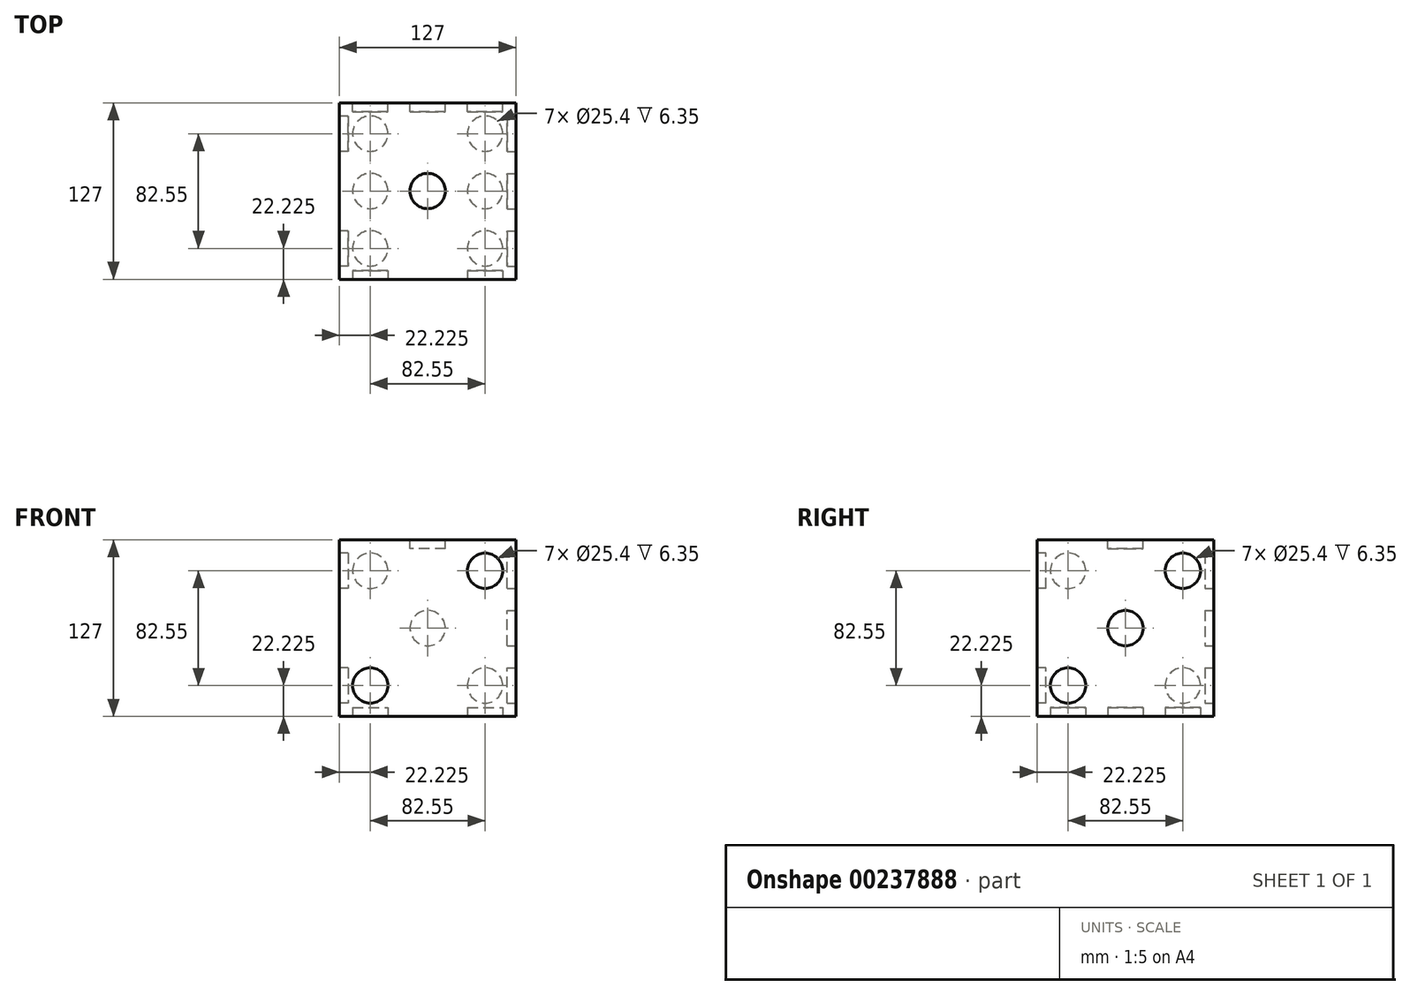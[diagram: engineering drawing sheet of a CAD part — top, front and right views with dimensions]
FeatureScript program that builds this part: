
annotation { "Feature Type Name" : "Feature", "Feature Type Description" : "" }
export const myFeature = defineFeature(function(context is Context, id is Id, definition is map)
    precondition{}
    {
        {
            var Q0;
            Q0=qCreatedBy(makeId("Top.planeOp"),FACE);
            var sketch = newSketch(context, id + "F0", { "sketchPlane" : qUnion([Q0])});
            skLineSegment(sketch, "E0.bottom", {"start": v(0, 0) * mm, "end": v(127, 0) * mm});
            skLineSegment(sketch, "E0.top", {"start": v(0, 127) * mm, "end": v(127, 127) * mm});
            skLineSegment(sketch, "E0.left", {"start": v(0, 0) * mm, "end": v(0, 127) * mm});
            skLineSegment(sketch, "E0.right", {"start": v(127, 0) * mm, "end": v(127, 127) * mm});
            skSolve(sketch);
        }
        {
            var Q0;
            Q0=makeQuery(id+"F0.imprint","IMPRINT",FACE,{"disambiguationData":[TD([[makeQuery(id+"F0.imprint","IMPRINT",EDGE,{"derivedFrom":sQuery(id+"F0.wireOp",EDGE,"E0.bottom")}),1.0]])]});
            extrude(context, id + "F1", {"entities" : qUnion([Q0]), "depth" : 127 * mm});
        }
        {
            var Q0;
            Q0=makeQuery(id+"F1.opExtrude","CAP_FACE",FACE,{"disambiguationData":[OSD([sQuery(id+"F0.wireOp",EDGE,"E0.bottom"),sQuery(id+"F0.wireOp",EDGE,"E0.top"),sQuery(id+"F0.wireOp",EDGE,"E0.left"),sQuery(id+"F0.wireOp",EDGE,"E0.right")])],"isStart":false});
            var sketch = newSketch(context, id + "F2", { "sketchPlane" : qUnion([Q0])});
            skCircle(sketch, "E1", {"center": v(63.5, 63.5) * mm, "radius": 12.7 * mm});
            skSolve(sketch);
        }
        {
            var Q0;
            Q0=makeQuery(id+"F2.imprint","IMPRINT",FACE,{"disambiguationData":[TD([[makeQuery(id+"F2.imprint","IMPRINT",EDGE,{"derivedFrom":sQuery(id+"F2.wireOp",EDGE,"E1")}),1.0]])]});
            extrude(context, id + "F3", {"entities" : qUnion([Q0]), "operationType" : NewBodyOperationType.REMOVE, "oppositeDirection" : true, "depth" : 6.35 * mm});
        }
        {
            var Q0;
            Q0=makeQuery(id+"F1.opExtrude","SWEPT_FACE",FACE,{"disambiguationData":[OSD([sQuery(id+"F0.wireOp",EDGE,"E0.bottom")])]});
            var sketch = newSketch(context, id + "F4", { "sketchPlane" : qUnion([Q0])});
            skCircle(sketch, "E2", {"center": v(104.78, 104.78) * mm, "radius": 12.7 * mm});
            skCircle(sketch, "E3", {"center": v(22.23, 22.22) * mm, "radius": 12.7 * mm});
            skSolve(sketch);
        }
        {
            var Q0;
            Q0=makeQuery(id+"F4.imprint","IMPRINT",FACE,{"disambiguationData":[TD([[makeQuery(id+"F4.imprint","IMPRINT",EDGE,{"derivedFrom":sQuery(id+"F4.wireOp",EDGE,"E3")}),1.0]])]});
            var Q1;
            Q1=makeQuery(id+"F4.imprint","IMPRINT",FACE,{"disambiguationData":[TD([[makeQuery(id+"F4.imprint","IMPRINT",EDGE,{"derivedFrom":sQuery(id+"F4.wireOp",EDGE,"E2")}),1.0]])]});
            extrude(context, id + "F5", {"entities" : qUnion([Q0, Q1]), "operationType" : NewBodyOperationType.REMOVE, "oppositeDirection" : true, "depth" : 6.35 * mm});
        }
        {
            var Q0;
            Q0=makeQuery(id+"F1.opExtrude","SWEPT_FACE",FACE,{"disambiguationData":[OSD([sQuery(id+"F0.wireOp",EDGE,"E0.left")])]});
            var sketch = newSketch(context, id + "F6", { "sketchPlane" : qUnion([Q0])});
            skCircle(sketch, "E4", {"center": v(-104.78, 22.22) * mm, "radius": 12.7 * mm});
            skCircle(sketch, "E5", {"center": v(-104.78, 104.78) * mm, "radius": 12.7 * mm});
            skCircle(sketch, "E6", {"center": v(-22.23, 104.78) * mm, "radius": 12.7 * mm});
            skCircle(sketch, "E7", {"center": v(-22.23, 22.22) * mm, "radius": 12.7 * mm});
            skSolve(sketch);
        }
        {
            var Q0;
            Q0=makeQuery(id+"F6.imprint","IMPRINT",FACE,{"disambiguationData":[TD([[makeQuery(id+"F6.imprint","IMPRINT",EDGE,{"derivedFrom":sQuery(id+"F6.wireOp",EDGE,"E5")}),1.0]])]});
            var Q1;
            Q1=makeQuery(id+"F6.imprint","IMPRINT",FACE,{"disambiguationData":[TD([[makeQuery(id+"F6.imprint","IMPRINT",EDGE,{"derivedFrom":sQuery(id+"F6.wireOp",EDGE,"E6")}),1.0]])]});
            var Q2;
            Q2=makeQuery(id+"F6.imprint","IMPRINT",FACE,{"disambiguationData":[TD([[makeQuery(id+"F6.imprint","IMPRINT",EDGE,{"derivedFrom":sQuery(id+"F6.wireOp",EDGE,"E7")}),1.0]])]});
            var Q3;
            Q3=makeQuery(id+"F6.imprint","IMPRINT",FACE,{"disambiguationData":[TD([[makeQuery(id+"F6.imprint","IMPRINT",EDGE,{"derivedFrom":sQuery(id+"F6.wireOp",EDGE,"E4")}),1.0]])]});
            var Q4;
            Q4=sQuery(id+"F6.wireOp",EDGE,"E5");
            extrude(context, id + "F7", {"entities" : qUnion([Q0, Q1, Q2, Q3]), "operationType" : NewBodyOperationType.REMOVE, "surfaceEntities" : qUnion([Q4]), "oppositeDirection" : true, "depth" : 6.35 * mm});
        }
        {
            var Q0;
            Q0=makeQuery(id+"F1.opExtrude","CAP_FACE",FACE,{"disambiguationData":[OSD([sQuery(id+"F0.wireOp",EDGE,"E0.bottom"),sQuery(id+"F0.wireOp",EDGE,"E0.top"),sQuery(id+"F0.wireOp",EDGE,"E0.left"),sQuery(id+"F0.wireOp",EDGE,"E0.right")])],"isStart":true});
            var sketch = newSketch(context, id + "F8", { "sketchPlane" : qUnion([Q0])});
            skCircle(sketch, "E8", {"center": v(22.23, -104.78) * mm, "radius": 12.7 * mm});
            skCircle(sketch, "E9", {"center": v(104.78, -22.23) * mm, "radius": 12.7 * mm});
            skCircle(sketch, "E10", {"center": v(104.78, -63.5) * mm, "radius": 12.7 * mm});
            skCircle(sketch, "E11", {"center": v(104.77, -104.78) * mm, "radius": 12.7 * mm});
            skCircle(sketch, "E12", {"center": v(22.23, -63.5) * mm, "radius": 12.7 * mm});
            skCircle(sketch, "E13", {"center": v(22.23, -22.23) * mm, "radius": 12.7 * mm});
            skLineSegment(sketch, "E14.0.0", {"start": v(0, -127) * mm, "end": v(127, -127) * mm});
            skLineSegment(sketch, "E14.0.1", {"start": v(127, -127) * mm, "end": v(127, 0) * mm});
            skLineSegment(sketch, "E14.0.2", {"start": v(127, 0) * mm, "end": v(0, 0) * mm});
            skLineSegment(sketch, "E14.0.3", {"start": v(0, 0) * mm, "end": v(0, -127) * mm});
            skSolve(sketch);
        }
        {
            var Q0;
            Q0=makeQuery(id+"F8.imprint","IMPRINT",FACE,{"disambiguationData":[TD([[makeQuery(id+"F8.imprint","IMPRINT",EDGE,{"derivedFrom":sQuery(id+"F8.wireOp",EDGE,"E13")}),1.0]])]});
            var Q1;
            Q1=makeQuery(id+"F8.imprint","IMPRINT",FACE,{"disambiguationData":[TD([[makeQuery(id+"F8.imprint","IMPRINT",EDGE,{"derivedFrom":sQuery(id+"F8.wireOp",EDGE,"E12")}),1.0]])]});
            var Q2;
            Q2=makeQuery(id+"F8.imprint","IMPRINT",FACE,{"disambiguationData":[TD([[makeQuery(id+"F8.imprint","IMPRINT",EDGE,{"derivedFrom":sQuery(id+"F8.wireOp",EDGE,"E8")}),1.0]])]});
            var Q3;
            Q3=makeQuery(id+"F8.imprint","IMPRINT",FACE,{"disambiguationData":[TD([[makeQuery(id+"F8.imprint","IMPRINT",EDGE,{"derivedFrom":sQuery(id+"F8.wireOp",EDGE,"E11")}),1.0]])]});
            var Q4;
            Q4=makeQuery(id+"F8.imprint","IMPRINT",FACE,{"disambiguationData":[TD([[makeQuery(id+"F8.imprint","IMPRINT",EDGE,{"derivedFrom":sQuery(id+"F8.wireOp",EDGE,"E10")}),1.0]])]});
            var Q5;
            Q5=makeQuery(id+"F8.imprint","IMPRINT",FACE,{"disambiguationData":[TD([[makeQuery(id+"F8.imprint","IMPRINT",EDGE,{"derivedFrom":sQuery(id+"F8.wireOp",EDGE,"E9")}),1.0]])]});
            extrude(context, id + "F9", {"entities" : qUnion([Q0, Q1, Q2, Q3, Q4, Q5]), "operationType" : NewBodyOperationType.REMOVE, "oppositeDirection" : true, "depth" : 6.35 * mm});
        }
        {
            var Q0;
            Q0=makeQuery(id+"F1.opExtrude","SWEPT_FACE",FACE,{"disambiguationData":[OSD([sQuery(id+"F0.wireOp",EDGE,"E0.right")])]});
            var sketch = newSketch(context, id + "F10", { "sketchPlane" : qUnion([Q0])});
            skCircle(sketch, "E15", {"center": v(104.77, 104.78) * mm, "radius": 12.7 * mm});
            skCircle(sketch, "E16", {"center": v(22.22, 22.22) * mm, "radius": 12.7 * mm});
            skCircle(sketch, "E17", {"center": v(63.5, 63.5) * mm, "radius": 12.7 * mm});
            skLineSegment(sketch, "E18", {"start": v(0, 0) * mm, "end": v(127, 127) * mm, "construction": true});
            skSolve(sketch);
        }
        {
            var Q0;
            Q0=makeQuery(id+"F10.imprint","IMPRINT",FACE,{"disambiguationData":[TD([[makeQuery(id+"F10.imprint","IMPRINT",EDGE,{"derivedFrom":sQuery(id+"F10.wireOp",EDGE,"E16")}),1.0]])]});
            var Q1;
            Q1=makeQuery(id+"F10.imprint","IMPRINT",FACE,{"disambiguationData":[TD([[makeQuery(id+"F10.imprint","IMPRINT",EDGE,{"derivedFrom":sQuery(id+"F10.wireOp",EDGE,"E17")}),1.0]])]});
            var Q2;
            Q2=makeQuery(id+"F10.imprint","IMPRINT",FACE,{"disambiguationData":[TD([[makeQuery(id+"F10.imprint","IMPRINT",EDGE,{"derivedFrom":sQuery(id+"F10.wireOp",EDGE,"E15")}),1.0]])]});
            extrude(context, id + "F11", {"entities" : qUnion([Q0, Q1, Q2]), "operationType" : NewBodyOperationType.REMOVE, "oppositeDirection" : true, "depth" : 6.35 * mm});
        }
        {
            var Q0;
            Q0=makeQuery(id+"F1.opExtrude","SWEPT_FACE",FACE,{"disambiguationData":[OSD([sQuery(id+"F0.wireOp",EDGE,"E0.top")])]});
            var sketch = newSketch(context, id + "F12", { "sketchPlane" : qUnion([Q0])});
            skCircle(sketch, "E19", {"center": v(-104.77, 22.22) * mm, "radius": 12.7 * mm});
            skCircle(sketch, "E20", {"center": v(-104.77, 104.78) * mm, "radius": 12.7 * mm});
            skCircle(sketch, "E21", {"center": v(-22.23, 104.78) * mm, "radius": 12.7 * mm});
            skCircle(sketch, "E22", {"center": v(-22.23, 22.22) * mm, "radius": 12.7 * mm});
            skCircle(sketch, "E23", {"center": v(-63.5, 63.5) * mm, "radius": 12.7 * mm});
            skSolve(sketch);
        }
        {
            var Q0;
            Q0=makeQuery(id+"F12.imprint","IMPRINT",FACE,{"disambiguationData":[TD([[makeQuery(id+"F12.imprint","IMPRINT",EDGE,{"derivedFrom":sQuery(id+"F12.wireOp",EDGE,"E20")}),1.0]])]});
            var Q1;
            Q1=makeQuery(id+"F12.imprint","IMPRINT",FACE,{"disambiguationData":[TD([[makeQuery(id+"F12.imprint","IMPRINT",EDGE,{"derivedFrom":sQuery(id+"F12.wireOp",EDGE,"E23")}),1.0]])]});
            var Q2;
            Q2=makeQuery(id+"F12.imprint","IMPRINT",FACE,{"disambiguationData":[TD([[makeQuery(id+"F12.imprint","IMPRINT",EDGE,{"derivedFrom":sQuery(id+"F12.wireOp",EDGE,"E19")}),1.0]])]});
            var Q3;
            Q3=makeQuery(id+"F12.imprint","IMPRINT",FACE,{"disambiguationData":[TD([[makeQuery(id+"F12.imprint","IMPRINT",EDGE,{"derivedFrom":sQuery(id+"F12.wireOp",EDGE,"E22")}),1.0]])]});
            var Q4;
            Q4=makeQuery(id+"F12.imprint","IMPRINT",FACE,{"disambiguationData":[TD([[makeQuery(id+"F12.imprint","IMPRINT",EDGE,{"derivedFrom":sQuery(id+"F12.wireOp",EDGE,"E21")}),1.0]])]});
            extrude(context, id + "F13", {"entities" : qUnion([Q0, Q1, Q2, Q3, Q4]), "operationType" : NewBodyOperationType.REMOVE, "oppositeDirection" : true, "depth" : 6.35 * mm});
        }
    });
